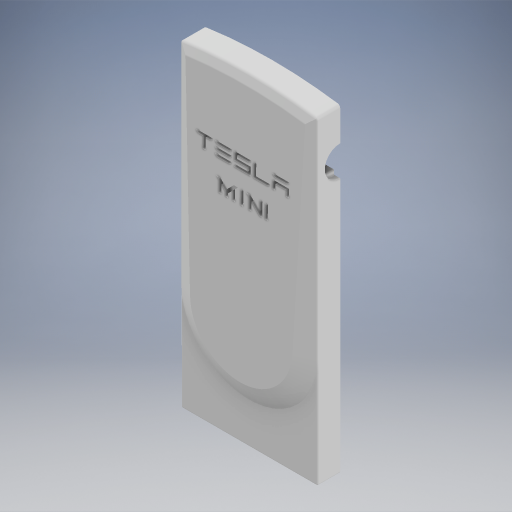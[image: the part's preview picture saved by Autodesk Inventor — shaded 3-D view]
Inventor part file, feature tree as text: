
AUTODESK INVENTOR PART (.ipt)
format: ipt  version: 2023.2 (Build 272271000, 271)  size: 1,128,448 bytes
history: native  units: in
note: dims shown in document units (in); Inventor stores cm internally (conversion verified against a paired STEP export)
features: extrude x11, sketch x11, fillet x5, chamfer x1, other x1
ambient origin geometry x8: Origin, YZ Plane, XZ Plane, XY Plane, X Axis, Y Axis, Z Axis, Center Point
bodies: Solid1 (feature_tree)
feature tree (29):
  extrude  "Extrusion1"  Depth=4.1339in
  extrude  "Extrusion2"  Depth=0.5906in TaperAngle=0.0deg
  chamfer  "Chamfer1"  Distance=0.1181in
  fillet  "Fillet1"  Radius=0.0394in
  fillet  "Fillet2"  Radius=0.6299in
  extrude  "Extrusion4"  Depth=0.3937in TaperAngle=0.0deg
  extrude  "Extrusion5"  Depth=0.3937in
  extrude  "Extrusion6"  Depth=0.5906in
  extrude  "Extrusion8"  Depth=0.0787in TaperAngle=0.0deg
  fillet  "Fillet3"  Radius=3.937in
  extrude  "Extrusion9"  Depth=0.1969in
  fillet  "Fillet4"  Radius=0.1969in
  extrude  "Extrusion10"  Depth=0.1969in
  extrude  "Extrusion11"  Depth=0.1969in
  fillet  "Fillet5"  Radius=0.1969in
  extrude  "Extrusion15"  Depth=0.1575in TaperAngle=0.0deg
  extrude  "Extrusion16"  Depth=0.0787in
  sketch  "Sketch1"  dims[d1=1.7717in d2=4.1339in]
  other  "Image1"
  sketch  "Sketch2"  dims[d24=5.9055in d25=0.5906in d26=0.0in]
  sketch  "Sketch4"  dims[d27=9.2917in]
  sketch  "Sketch5"  dims[d28=1.4706in]
  sketch  "Sketch6"  dims[d30=15.4284in]
  sketch  "Sketch7"  dims[d47=2.7165in]
  sketch  "Sketch8"  dims[d48=2.7165in]
  sketch  "Sketch9"  dims[d49=5.9055in d50=0.1181in d51=-0.4466in]
  sketch  "Sketch10"  dims[d52=0.1575in d53=3.1614in d54=45.0deg d67=0.0394in d71=0.6299in]
  sketch  "Sketch14"  dims[d72=0.315in d73=0.3937in d74=0.0in]
  sketch  "Sketch15"  dims[d75=0.0197in d76=0.3937in d77=0.5906in d79=0.0787in d80=0.0in d81=3.937in d82=0.0in d83=0.1969in d86=0.1969in d87=0.1969in d88=0.1969in d89=0.1969in d90=0.1575in d91=0.0in d92=0.0787in d93=0.1575in d94=0.3937in d95=0.1575in d96=0.3937in d97=0.315in d98=0.1575in d99=0.315in d100=0.1575in d101=0.1575in d102=0.0in d103=0.0787in d104=0.1181in d105=0.2756in d106=0.0591in d107=0.1378in d108=0.0in d118=0.1575in d119=0.0in d131=0.0787in d132=0.5512in d133=0.1378in d134=0.0787in d135=0.3937in d136=0.1378in d137=0.0787in d138=0.0in d139=1.1811in d140=0.2953in d141=0.5906in d142=0.7874in d143=0.3937in d144=0.0in d78=0.0in d84=0.0344in d123=0.0197in d124=0.0344in d125=0.0197in d126=0.0344in]
